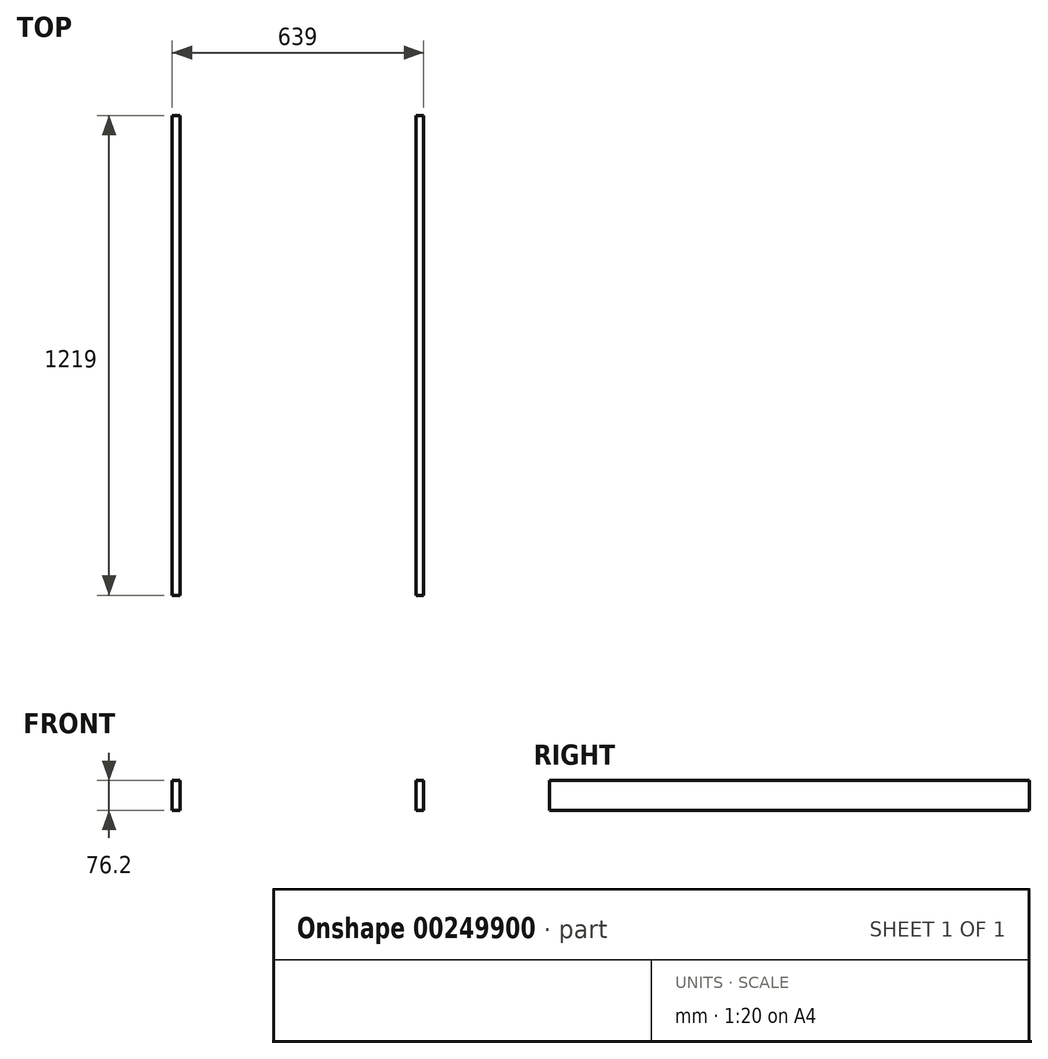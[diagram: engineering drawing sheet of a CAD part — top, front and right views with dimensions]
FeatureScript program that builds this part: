
annotation { "Feature Type Name" : "Feature", "Feature Type Description" : "" }
export const myFeature = defineFeature(function(context is Context, id is Id, definition is map)
    precondition{}
    {
        {
            var Q0;
            Q0=qCreatedBy(makeId("Front.planeOp"),FACE);
            var sketch = newSketch(context, id + "F0", { "sketchPlane" : qUnion([Q0])});
            skLineSegment(sketch, "E0.bottom", {"start": v(300, 0) * mm, "end": v(319.5, 0) * mm});
            skLineSegment(sketch, "E0.top", {"start": v(300, -76.2) * mm, "end": v(319.5, -76.2) * mm});
            skLineSegment(sketch, "E0.left", {"start": v(300, 0) * mm, "end": v(300, -76.2) * mm});
            skLineSegment(sketch, "E0.right", {"start": v(319.5, 0) * mm, "end": v(319.5, -76.2) * mm});
            skLineSegment(sketch, "E1.MirrorCS", {"start": v(-300, 0) * mm, "end": v(-319.5, 0) * mm});
            skLineSegment(sketch, "E2.MirrorCS", {"start": v(-300, -76.2) * mm, "end": v(-319.5, -76.2) * mm});
            skLineSegment(sketch, "E3.MirrorCS", {"start": v(-319.5, 0) * mm, "end": v(-319.5, -76.2) * mm});
            skLineSegment(sketch, "E4.MirrorCS", {"start": v(-300, 0) * mm, "end": v(-300, -76.2) * mm});
            skSolve(sketch);
        }
        {
            var Q0;
            Q0=makeQuery(id+"F0.imprint","IMPRINT",FACE,{"disambiguationData":[TD([[makeQuery(id+"F0.imprint","IMPRINT",EDGE,{"derivedFrom":sQuery(id+"F0.wireOp",EDGE,"E0.bottom")}),-1.0]])]});
            var Q1;
            Q1=makeQuery(id+"F0.imprint","IMPRINT",FACE,{"disambiguationData":[TD([[makeQuery(id+"F0.imprint","IMPRINT",EDGE,{"derivedFrom":sQuery(id+"F0.wireOp",EDGE,"E1.MirrorCS")}),1.0]])]});
            extrude(context, id + "F1", {"entities" : qUnion([Q0, Q1]), "oppositeDirection" : true, "depth" : 1219 * mm});
        }
    });
